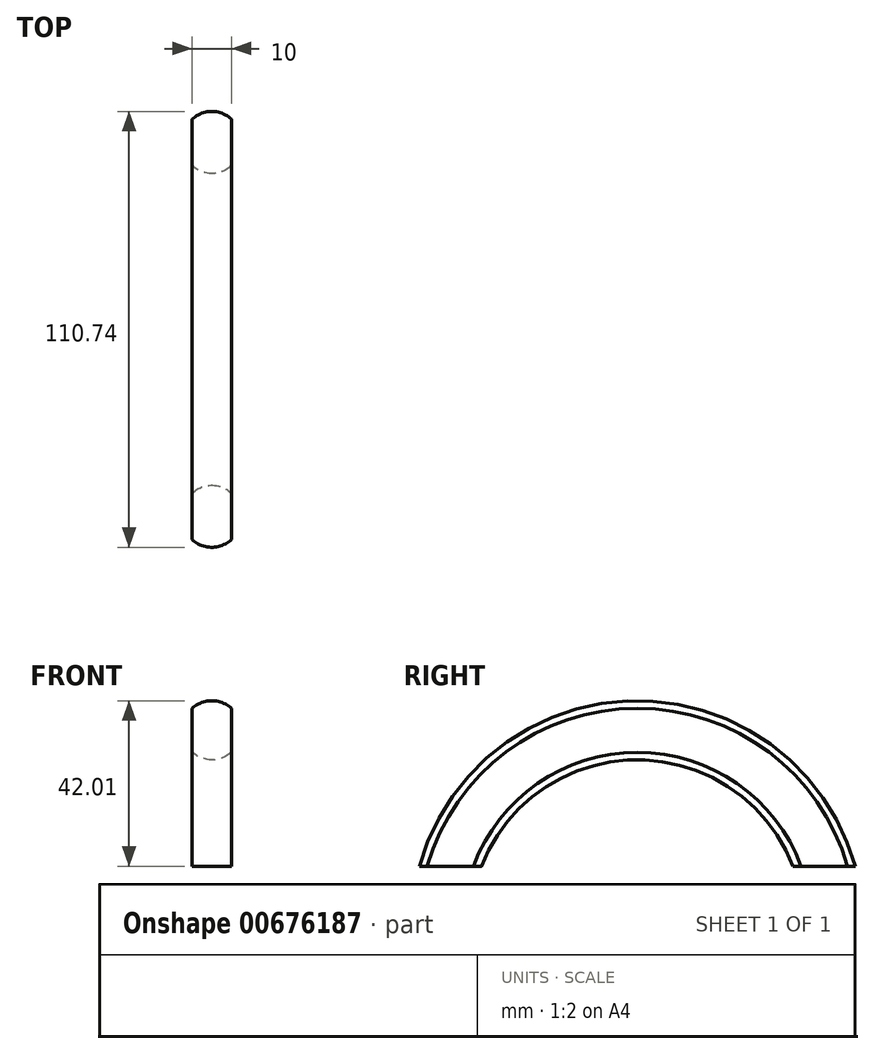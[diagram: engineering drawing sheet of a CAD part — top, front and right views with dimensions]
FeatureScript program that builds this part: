
annotation { "Feature Type Name" : "Feature", "Feature Type Description" : "" }
export const myFeature = defineFeature(function(context is Context, id is Id, definition is map)
    precondition{}
    {
        {
            var Q0;
            Q0=qCreatedBy(makeId("Top.planeOp"),FACE);
            var sketch = newSketch(context, id + "F0", { "sketchPlane" : qUnion([Q0])});
            skCircle(sketch, "E0", {"center": v(0, 50) * mm, "radius": 7.5 * mm});
            skSolve(sketch);
        }
        {
            var Q0;
            Q0=qCreatedBy(makeId("Right.planeOp"),FACE);
            var sketch = newSketch(context, id + "F1", { "sketchPlane" : qUnion([Q0])});
            skCircle(sketch, "E1", {"center": v(0, 0) * mm, "radius": 49.98 * mm});
            skSolve(sketch);
        }
        {
            var Q0;
            Q0=makeQuery(id+"F0.imprint","IMPRINT",FACE,{"disambiguationData":[TD([[makeQuery(id+"F0.imprint","IMPRINT",EDGE,{"derivedFrom":sQuery(id+"F0.wireOp",EDGE,"E0")}),1.0]])]});
            var Q1;
            Q1=sQuery(id+"F1.wireOp",EDGE,"E1");
            revolve(context, id + "F2", {"entities" : qUnion([Q0]), "axis" : qUnion([Q1]), "revolveType" : RevolveType.FULL});
        }
        {
            var Q0;
            Q0=qCreatedBy(makeId("Right.planeOp"),FACE);
            var sketch = newSketch(context, id + "F3", { "sketchPlane" : qUnion([Q0])});
            skLineSegment(sketch, "E2.bottom", {"start": v(-67.46, 15.49) * mm, "end": v(72.5, 15.49) * mm});
            skLineSegment(sketch, "E2.top", {"start": v(-67.46, -72.13) * mm, "end": v(72.5, -72.13) * mm});
            skLineSegment(sketch, "E2.left", {"start": v(-67.46, 15.49) * mm, "end": v(-67.46, -72.13) * mm});
            skLineSegment(sketch, "E2.right", {"start": v(72.5, 15.49) * mm, "end": v(72.5, -72.13) * mm});
            skSolve(sketch);
        }
        {
            var Q0;
            Q0 = qSketchRegion(id + "F3", true);
            extrude(context, id + "F4", {"entities" : qUnion([Q0]), "operationType" : NewBodyOperationType.REMOVE, "oppositeDirection" : true, "depth" : 25 * mm, "offsetDistance" : 25 * mm});
        }
        {
            var Q0;
            Q0 = qSketchRegion(id + "F3", true);
            extrude(context, id + "F5", {"entities" : qUnion([Q0]), "operationType" : NewBodyOperationType.REMOVE, "depth" : 44.2 * mm, "offsetDistance" : 25 * mm});
        }
        {
            var Q0;
            Q0=qCreatedBy(makeId("Top.planeOp"),FACE);
            var sketch = newSketch(context, id + "F6", { "sketchPlane" : qUnion([Q0])});
            skLineSegment(sketch, "E3.bottom", {"start": v(5, 87.07) * mm, "end": v(45.24, 87.07) * mm});
            skLineSegment(sketch, "E3.top", {"start": v(5, -87.07) * mm, "end": v(45.24, -87.07) * mm});
            skLineSegment(sketch, "E3.left", {"start": v(5, 87.07) * mm, "end": v(5, -87.07) * mm});
            skLineSegment(sketch, "E3.right", {"start": v(45.24, 87.07) * mm, "end": v(45.24, -87.07) * mm});
            skLineSegment(sketch, "E4.bottom", {"start": v(-5, 71.13) * mm, "end": v(-38.9, 71.13) * mm});
            skLineSegment(sketch, "E4.top", {"start": v(-5, -76.8) * mm, "end": v(-38.9, -76.8) * mm});
            skLineSegment(sketch, "E4.left", {"start": v(-5, 71.13) * mm, "end": v(-5, -76.8) * mm});
            skLineSegment(sketch, "E4.right", {"start": v(-38.9, 71.13) * mm, "end": v(-38.9, -76.8) * mm});
            skSolve(sketch);
        }
        {
            var Q0;
            Q0 = qSketchRegion(id + "F6", true);
            var Q1;
            Q1=makeQuery(id+"F6.imprint","IMPRINT",FACE,{"disambiguationData":[TD([[makeQuery(id+"F6.imprint","IMPRINT",EDGE,{"derivedFrom":sQuery(id+"F6.wireOp",EDGE,"E4.bottom")}),1.0]])]});
            extrude(context, id + "F7", {"entities" : qUnion([Q0, Q1]), "operationType" : NewBodyOperationType.REMOVE, "depth" : 78.9 * mm, "offsetDistance" : 25 * mm});
        }
    });
